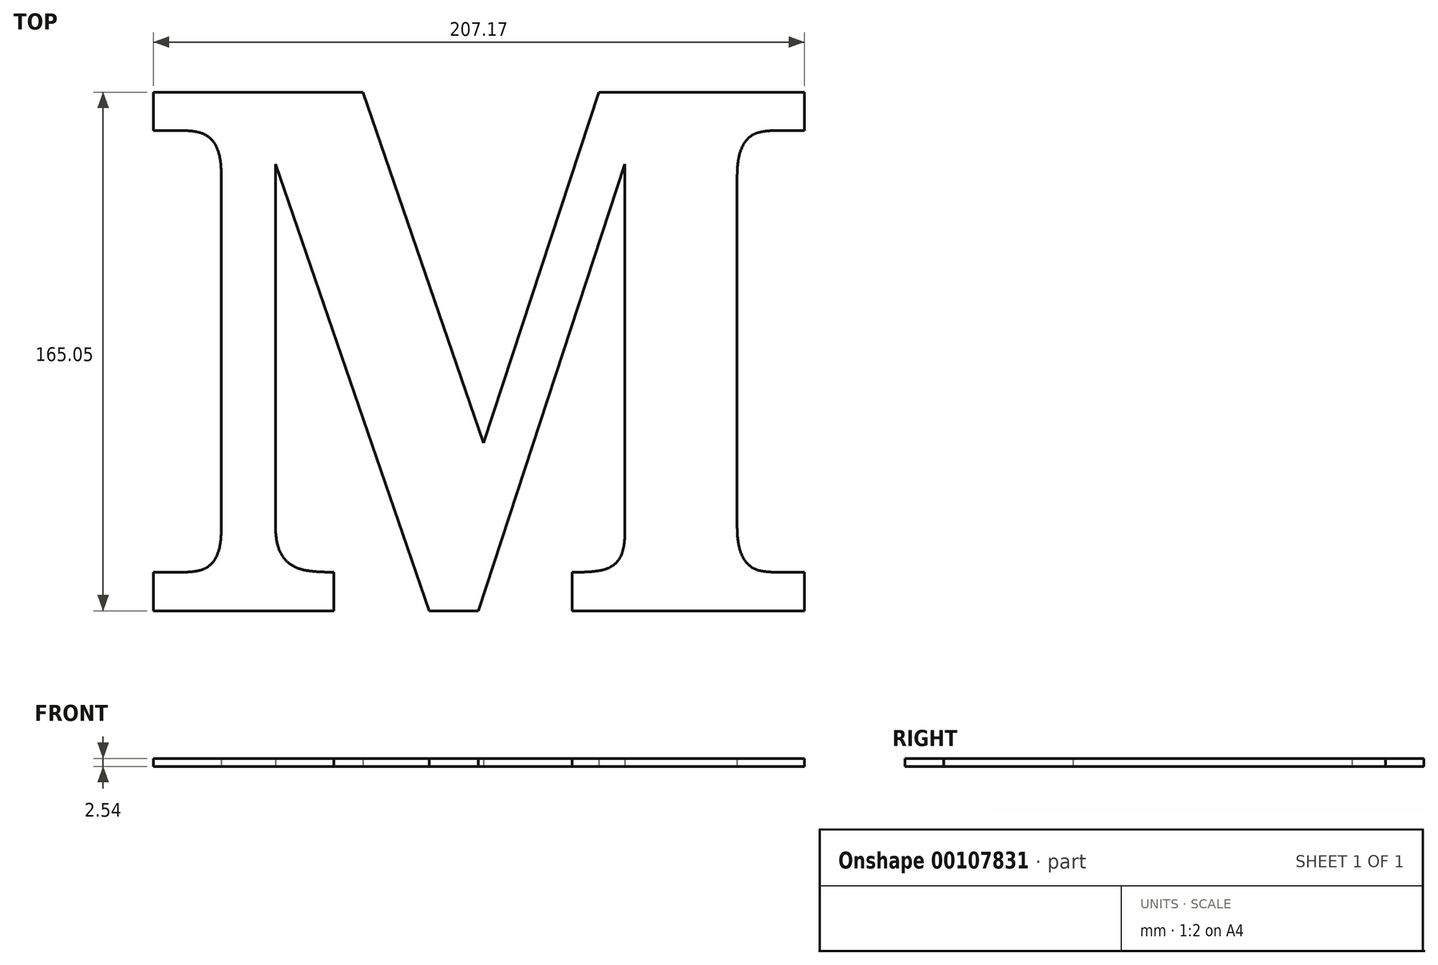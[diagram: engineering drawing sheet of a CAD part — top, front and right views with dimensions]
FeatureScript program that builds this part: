
annotation { "Feature Type Name" : "Feature", "Feature Type Description" : "" }
export const myFeature = defineFeature(function(context is Context, id is Id, definition is map)
    precondition{}
    {
        {
            var Q0;
            Q0=qCreatedBy(makeId("Top.planeOp"),FACE);
            var sketch = newSketch(context, id + "F0", { "sketchPlane" : qUnion([Q0])});
            skText(sketch, "E0", { "text": "M", "fontName": "NotoSerif-Bold.ttf"});
            const initialGuessF0  = {"E0": [0, -0.16646, 1, 0, 0.16646]};
            skSetInitialGuess(sketch, initialGuessF0);
            skSolve(sketch);
        }
        {
            var Q0;
            Q0 = qSketchRegion(id + "F0", true);
            extrude(context, id + "F1", {"entities" : qUnion([Q0]), "depth" : 2.54 * mm});
        }
    });
